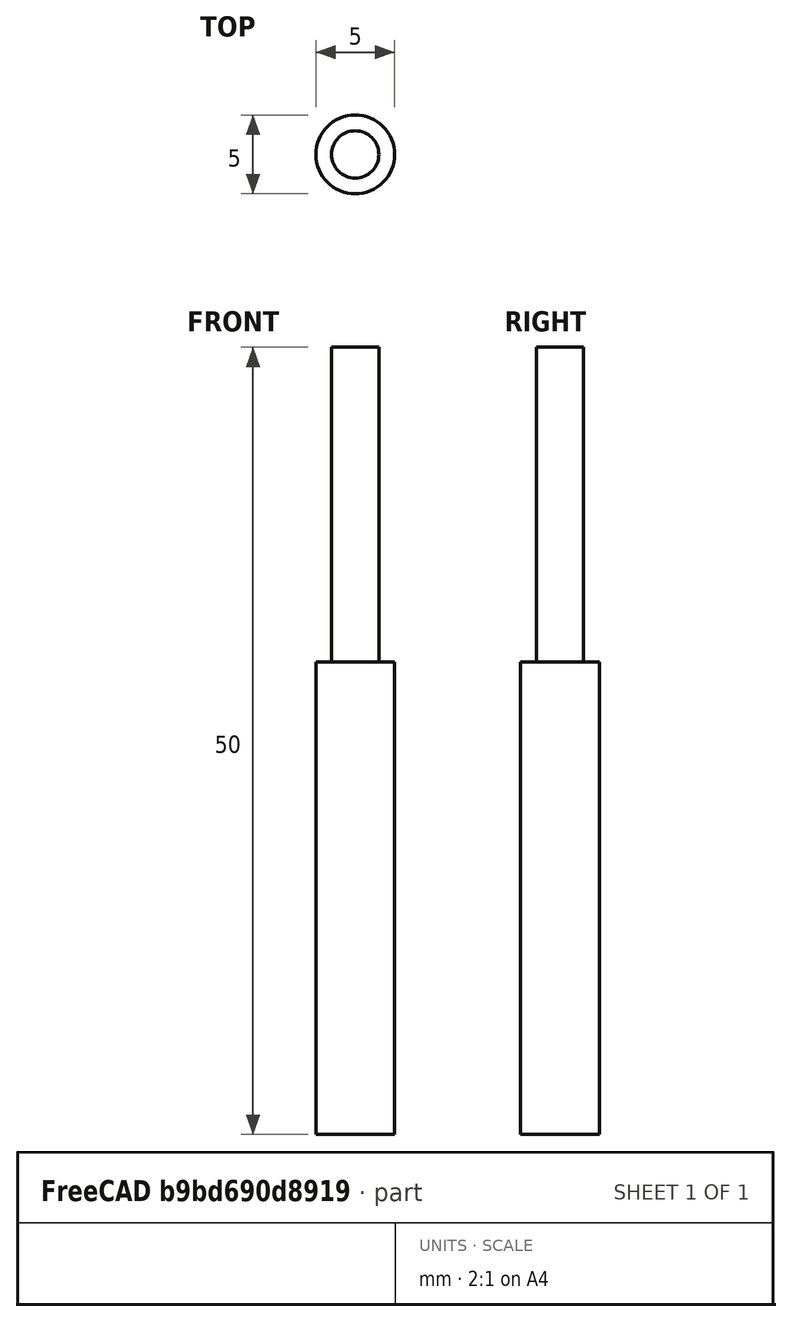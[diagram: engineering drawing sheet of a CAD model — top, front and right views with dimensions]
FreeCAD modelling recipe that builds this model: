
FCSTD DOCUMENT  (FreeCAD 0.20R28439 +1 (Git))
Label: endmill
License: All rights reserved
LicenseURL: http://en.wikipedia.org/wiki/All_rights_reserved
objects: Sketcher::SketchObject×1, PartDesign::Revolution×1, App::FeaturePython×1, PartDesign::Body×1
note: 4 computed .brp shape members not serialized (recipe doc carries the construction recipe); baked Part::Feature solids carry a one-line shape summary decoded from their .brp

FEATURE [Sketcher::SketchObject] Sketch
  FullyConstrained = true
  MapMode = 5
  Placement = pos=(0,0,0) rot=(1,0,0;1.5708rad)
  Support = -> [XZ_Plane]
  expr: Constraints[10] = <<Attributes>>.Length
  expr: Constraints[16] = <<Attributes>>.ShankDiameter
  expr: Constraints[18] = <<Attributes>>.CuttingEdgeHeight
  expr: Constraints[9] = <<Attributes>>.Diameter
  sketch-geometry (8):
    g0: LineSegment StartX=0 StartY=50 StartZ=0 EndX=0 EndY=0 EndZ=0
    g1: LineSegment StartX=0 StartY=0 StartZ=0 EndX=2.5 EndY=0 EndZ=0
    g2: LineSegment StartX=2.5 StartY=0 StartZ=0 EndX=2.5 EndY=30 EndZ=0
    g3: LineSegment StartX=1.5 StartY=50 StartZ=0 EndX=0 EndY=50 EndZ=0
    g4: LineSegment StartX=2.5 StartY=0 StartZ=0 EndX=-2.5 EndY=0 EndZ=0
    g5: LineSegment StartX=1.5 StartY=29.99 StartZ=0 EndX=2.5 EndY=30 EndZ=0
    g6: LineSegment StartX=1.5 StartY=50 StartZ=0 EndX=1.5 EndY=29.99 EndZ=0
    g7: LineSegment StartX=-1.5 StartY=50 StartZ=0 EndX=1.5 EndY=50 EndZ=0
  constraints (21):
    c: Vertical(g0)
    c: Coincident(g0,g1)
    c: Horizontal(g1)
    c: Coincident(g1,g2)
    c: Vertical(g2)
    c: Horizontal(g3)
    c: Coincident(g0,g3)
    c: Coincident(g4,g1)
    c: Symmetric(g1,g4,g0)
    c: DistanceX(g4,g4) = 5
    c: DistanceY(g2,g3) = 50
    c: Coincident(g2,g5)
    c: Vertical(g6)
    c: Coincident(g3,g6)
    c: Symmetric(g7,g7,g0)
    c: Coincident(g7,g3)
    c: DistanceX(g7,g7) = 3
    c: Coincident(g5,g6)
    c: DistanceY(g2) = 30
    c: Coincident(g0,g-1)
    c: DistanceY(g5,g2) = 0.01
FEATURE [PartDesign::Revolution] Revolution
  AllowMultiFace = false
  Angle = 360
  Axis = (0,-2e-16,1)
  Base = (0,0,0)
  Placement = pos=(0,0,0) rot=(1,0,0;1.5708rad)
  Profile = -> Sketch
  ReferenceAxis = -> Sketch [V_Axis]
  Reversed = true
FEATURE [App::FeaturePython] PropertyBag  label="Attributes"  # WARN: FeaturePython — macro-defined, semantics opaque (R4)
  Chipload = 0
  CustomPropertyGroups = Attributes | Shape
  CuttingEdgeHeight = 30
  Diameter = 5
  Flutes = 0
  Length = 50
  Material = 0
  ShankDiameter = 3
  SpindleDirection = 0
FEATURE [PartDesign::Body] Body  label="Endmill"
  Group = -> [Sketch,Revolution,PropertyBag]
  Origin = -> Origin
  Tip = -> Revolution
